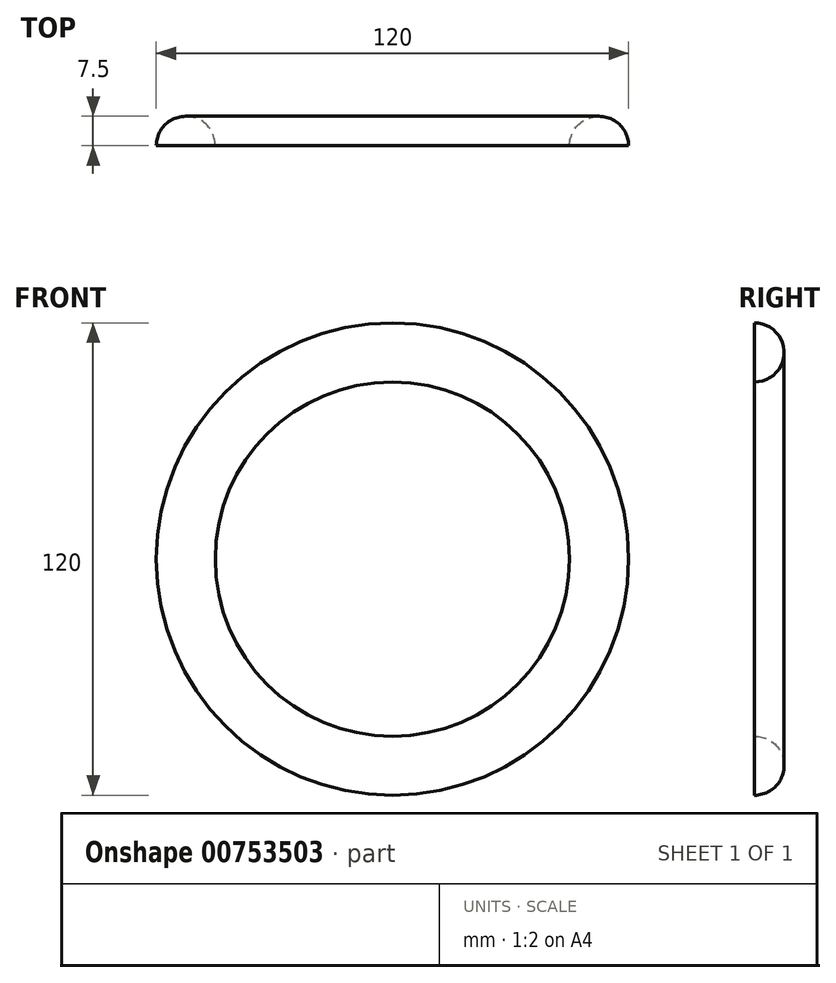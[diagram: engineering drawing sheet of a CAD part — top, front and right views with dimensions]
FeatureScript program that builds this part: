
annotation { "Feature Type Name" : "Feature", "Feature Type Description" : "" }
export const myFeature = defineFeature(function(context is Context, id is Id, definition is map)
    precondition{}
    {
        {
            var Q0;
            Q0=qCreatedBy(makeId("Top.planeOp"),FACE);
            var sketch = newSketch(context, id + "F0", { "sketchPlane" : qUnion([Q0])});
            skLineSegment(sketch, "E0", {"start": v(-71.28, 0) * mm, "end": v(76.2, 0) * mm});
            skPoint(sketch, "E1", {"position": v(-52.5, 0) * mm});
            skCircle(sketch, "E2", {"center": v(-52.5, 0) * mm, "radius": 7.5 * mm});
            skLineSegment(sketch, "E3", {"start": v(0, 49.24) * mm, "end": v(0, -56.32) * mm});
            skSolve(sketch);
        }
        {
            var Q0;
            {var subQ0=sQuery(id+"F0.wireOp",EDGE,"E2");var subQ1=sQuery(id+"F0.wireOp",EDGE,"E0");var subQ2=makeQuery(id+"F0.imprint","INTERSECT",VERTEX,{"disambiguationData":[OD(0.0)],"derivedFrom":[subQ1,subQ0]});Q0=makeQuery(id+"F0.imprint","IMPRINT",FACE,{"disambiguationData":[TD([[makeQuery(id+"F0.imprint","IMPRINT",EDGE,{"disambiguationData":[TD([[subQ2,-1.0]])],"derivedFrom":subQ1}),1.0]])]});}
            var Q1;
            Q1=sQuery(id+"F0.wireOp",EDGE,"E3");
            revolve(context, id + "F1", {"surfaceOperationType" : NewSurfaceOperationType.NEW, "entities" : qUnion([Q0]), "axis" : qUnion([Q1]), "revolveType" : RevolveType.FULL});
        }
    });
